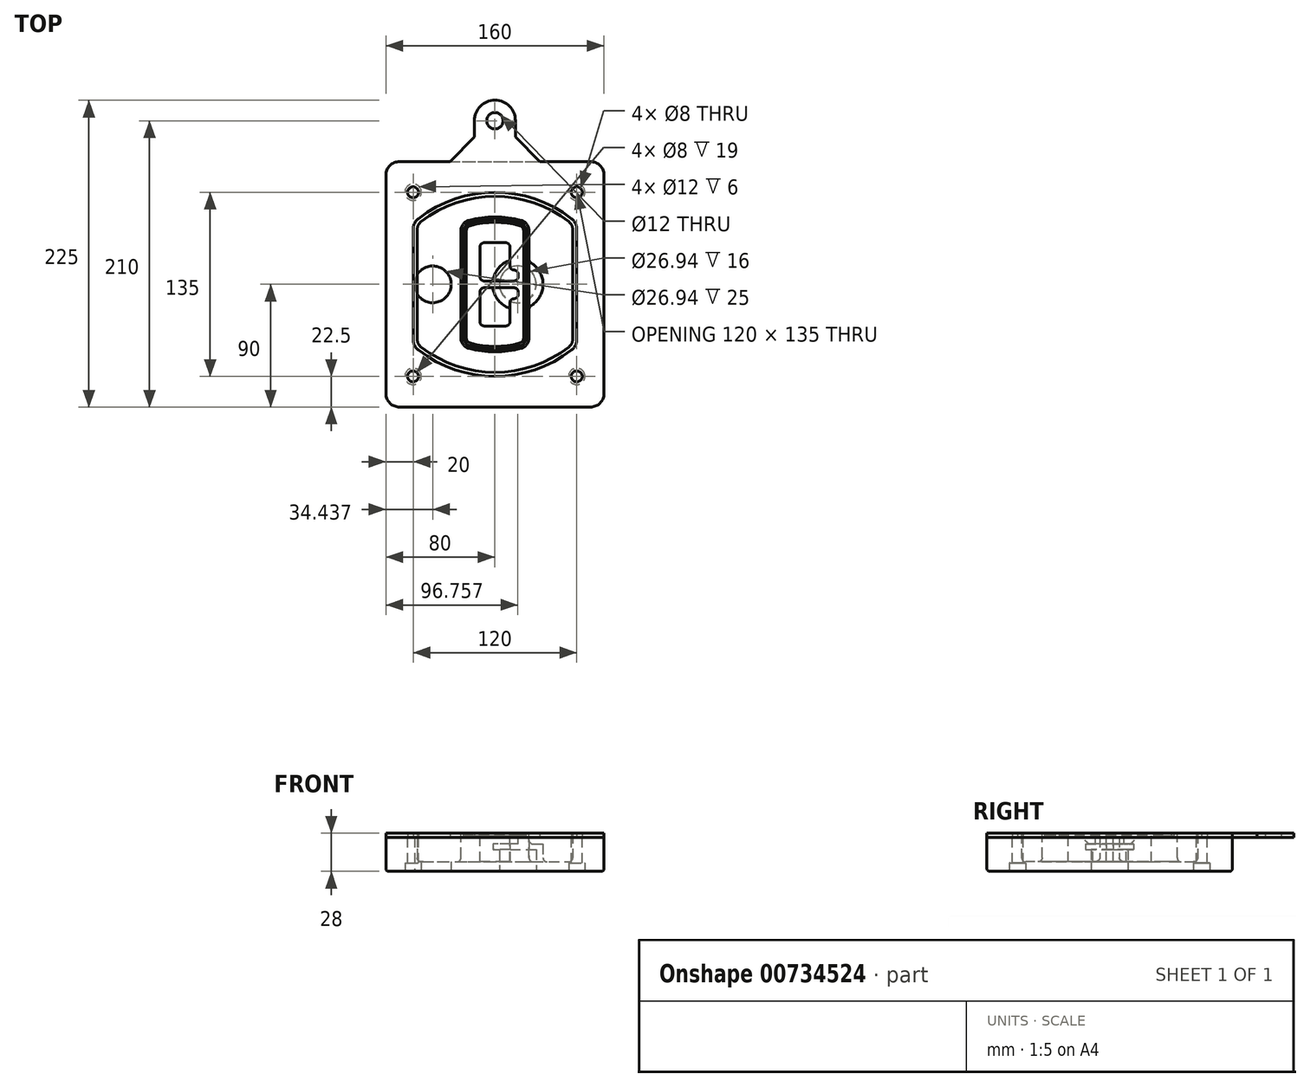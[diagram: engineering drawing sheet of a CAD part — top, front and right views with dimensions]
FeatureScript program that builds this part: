
annotation { "Feature Type Name" : "Feature", "Feature Type Description" : "" }
export const myFeature = defineFeature(function(context is Context, id is Id, definition is map)
    precondition{}
    {
        {
            var Q0;
            Q0=qCreatedBy(makeId("Top.planeOp"),FACE);
            var sketch = newSketch(context, id + "F0", { "sketchPlane" : qUnion([Q0])});
            skPoint(sketch, "E0.rect.middle", {"position": v(0, 0) * mm});
            skLineSegment(sketch, "E1.bottom", {"start": v(-70, -90) * mm, "end": v(70, -90) * mm});
            skLineSegment(sketch, "E1.top", {"start": v(-70, 90) * mm, "end": v(70, 90) * mm});
            skLineSegment(sketch, "E1.left", {"start": v(-80, -80) * mm, "end": v(-80, 80) * mm});
            skLineSegment(sketch, "E1.right", {"start": v(80, -80) * mm, "end": v(80, 80) * mm});
            skLineSegment(sketch, "E2", {"start": v(-80, 90) * mm, "end": v(80, -90) * mm, "construction": true});
            skLineSegment(sketch, "E3", {"start": v(80, 90) * mm, "end": v(-80, -90) * mm, "construction": true});
            skCircle(sketch, "E4", {"center": v(-60, 67.5) * mm, "radius": 4 * mm});
            skCircle(sketch, "E5", {"center": v(60, 67.5) * mm, "radius": 4 * mm});
            skCircle(sketch, "E6", {"center": v(60, -67.5) * mm, "radius": 4 * mm});
            skCircle(sketch, "E7", {"center": v(-60, -67.5) * mm, "radius": 4 * mm});
            skLineSegment(sketch, "E8", {"start": v(-60, 67.5) * mm, "end": v(60, 67.5) * mm, "construction": true});
            skLineSegment(sketch, "E9", {"start": v(60, 67.5) * mm, "end": v(60, -67.5) * mm, "construction": true});
            skLineSegment(sketch, "E10", {"start": v(60, -67.5) * mm, "end": v(-60, -67.5) * mm, "construction": true});
            skLineSegment(sketch, "E11", {"start": v(-60, -67.5) * mm, "end": v(-60, 67.5) * mm, "construction": true});
            skLineSegment(sketch, "E12", {"start": v(-60, 40.3) * mm, "end": v(-60, -40.3) * mm});
            skLineSegment(sketch, "E13", {"start": v(60, 40.3) * mm, "end": v(60, -40.3) * mm});
            skArc(sketch, "E14", {"start": v(56.15, 48.18) * mm, "mid": v(0, 67.5) * mm, "end": v(-56.15, 48.18) * mm});
            skArc(sketch, "E15", {"start": v(-56.15, -48.18) * mm, "mid": v(0, -67.5) * mm, "end": v(56.15, -48.18) * mm});
            skLineSegment(sketch, "E16", {"start": v(-60, 0) * mm, "end": v(60, 0) * mm, "construction": true});
            skPoint(sketch, "E17.visualSharp", {"position": v(-60, -45) * mm});
            skArc(sketch, "E17.filletArc", {"start": v(-60, -40.3) * mm, "mid": v(-58.99, -44.68) * mm, "end": v(-56.15, -48.18) * mm});
            skPoint(sketch, "E18.visualSharp", {"position": v(-60, 45) * mm});
            skArc(sketch, "E18.filletArc", {"start": v(-56.15, 48.18) * mm, "mid": v(-58.99, 44.68) * mm, "end": v(-60, 40.3) * mm});
            skPoint(sketch, "E19.visualSharp", {"position": v(60, 45) * mm});
            skArc(sketch, "E19.filletArc", {"start": v(60, 40.3) * mm, "mid": v(58.99, 44.68) * mm, "end": v(56.15, 48.18) * mm});
            skPoint(sketch, "E20.visualSharp", {"position": v(60, -45) * mm});
            skArc(sketch, "E20.filletArc", {"start": v(56.15, -48.18) * mm, "mid": v(58.99, -44.68) * mm, "end": v(60, -40.3) * mm});
            skPoint(sketch, "E21.visualSharp", {"position": v(-80, 90) * mm});
            skArc(sketch, "E21.filletArc", {"start": v(-70, 90) * mm, "mid": v(-77.07, 87.07) * mm, "end": v(-80, 80) * mm});
            skPoint(sketch, "E22.visualSharp", {"position": v(80, 90) * mm});
            skArc(sketch, "E22.filletArc", {"start": v(80, 80) * mm, "mid": v(77.07, 87.07) * mm, "end": v(70, 90) * mm});
            skPoint(sketch, "E23.visualSharp", {"position": v(80, -90) * mm});
            skArc(sketch, "E23.filletArc", {"start": v(70, -90) * mm, "mid": v(77.07, -87.07) * mm, "end": v(80, -80) * mm});
            skPoint(sketch, "E24.visualSharp", {"position": v(-80, -90) * mm});
            skArc(sketch, "E24.filletArc", {"start": v(-80, -80) * mm, "mid": v(-77.07, -87.07) * mm, "end": v(-70, -90) * mm});
            skArc(sketch, "E25.0", {"start": v(57, 40.3) * mm, "mid": v(56.3, 43.36) * mm, "end": v(54.3, 45.81) * mm});
            skLineSegment(sketch, "E25.1", {"start": v(57, 40.3) * mm, "end": v(57, -40.3) * mm});
            skArc(sketch, "E25.2", {"start": v(54.3, -45.81) * mm, "mid": v(56.3, -43.36) * mm, "end": v(57, -40.3) * mm});
            skArc(sketch, "E25.3", {"start": v(-54.3, -45.81) * mm, "mid": v(0, -64.5) * mm, "end": v(54.3, -45.81) * mm});
            skArc(sketch, "E25.4", {"start": v(-57, -40.3) * mm, "mid": v(-56.3, -43.36) * mm, "end": v(-54.3, -45.81) * mm});
            skArc(sketch, "E25.5", {"start": v(54.3, 45.81) * mm, "mid": v(0, 64.5) * mm, "end": v(-54.3, 45.81) * mm});
            skLineSegment(sketch, "E25.6", {"start": v(-57, 40.3) * mm, "end": v(-57, -40.3) * mm});
            skArc(sketch, "E25.7", {"start": v(-54.3, 45.81) * mm, "mid": v(-56.3, 43.36) * mm, "end": v(-57, 40.3) * mm});
            skArc(sketch, "E26.0", {"start": v(-58.62, 51.33) * mm, "mid": v(-62.58, 46.43) * mm, "end": v(-64, 40.3) * mm});
            skArc(sketch, "E26.1", {"start": v(58.62, 51.33) * mm, "mid": v(0, 71.5) * mm, "end": v(-58.62, 51.33) * mm});
            skArc(sketch, "E26.2", {"start": v(64, 40.3) * mm, "mid": v(62.58, 46.43) * mm, "end": v(58.62, 51.33) * mm});
            skLineSegment(sketch, "E26.3", {"start": v(64, 40.3) * mm, "end": v(64, -40.3) * mm});
            skArc(sketch, "E26.4", {"start": v(58.62, -51.33) * mm, "mid": v(62.58, -46.43) * mm, "end": v(64, -40.3) * mm});
            skLineSegment(sketch, "E26.5", {"start": v(-64, 40.3) * mm, "end": v(-64, -40.3) * mm});
            skArc(sketch, "E26.6", {"start": v(-58.62, -51.33) * mm, "mid": v(0, -71.5) * mm, "end": v(58.62, -51.33) * mm});
            skArc(sketch, "E26.7", {"start": v(-64, -40.3) * mm, "mid": v(-62.58, -46.43) * mm, "end": v(-58.62, -51.33) * mm});
            skSolve(sketch);
        }
        {
            var Q0;
            Q0=makeQuery(id+"F0.imprint","IMPRINT",FACE,{"disambiguationData":[TD([[makeQuery(id+"F0.imprint","IMPRINT",EDGE,{"derivedFrom":sQuery(id+"F0.wireOp",EDGE,"E1.bottom")}),1.0]])]});
            var Q1;
            Q1=makeQuery(id+"F0.imprint","IMPRINT",FACE,{"disambiguationData":[TD([[makeQuery(id+"F0.imprint","IMPRINT",EDGE,{"derivedFrom":sQuery(id+"F0.wireOp",EDGE,"E12")}),1.0]])]});
            var Q2;
            Q2=makeQuery(id+"F0.imprint","IMPRINT",FACE,{"disambiguationData":[TD([[makeQuery(id+"F0.imprint","IMPRINT",EDGE,{"derivedFrom":sQuery(id+"F0.wireOp",EDGE,"E25.0")}),1.0]])]});
            var Q3;
            Q3=makeQuery(id+"F0.imprint","IMPRINT",FACE,{"disambiguationData":[TD([[makeQuery(id+"F0.imprint","IMPRINT",EDGE,{"derivedFrom":sQuery(id+"F0.wireOp",EDGE,"E12")}),-1.0]])]});
            extrude(context, id + "F1", {"entities" : qUnion([Q0, Q1, Q2, Q3]), "oppositeDirection" : true, "depth" : 25 * mm});
        }
        {
            var Q0;
            Q0=makeQuery(id+"F0.imprint","IMPRINT",FACE,{"disambiguationData":[TD([[makeQuery(id+"F0.imprint","IMPRINT",EDGE,{"derivedFrom":sQuery(id+"F0.wireOp",EDGE,"E12")}),1.0]])]});
            extrude(context, id + "F2", {"entities" : qUnion([Q0]), "operationType" : NewBodyOperationType.ADD, "depth" : 3 * mm});
        }
        {
            var Q0;
            Q0=makeQuery(id+"F0.imprint","IMPRINT",FACE,{"disambiguationData":[TD([[makeQuery(id+"F0.imprint","IMPRINT",EDGE,{"derivedFrom":sQuery(id+"F0.wireOp",EDGE,"E25.0")}),1.0]])]});
            extrude(context, id + "F3", {"entities" : qUnion([Q0]), "operationType" : NewBodyOperationType.REMOVE, "oppositeDirection" : true, "depth" : 18 * mm});
        }
        {
            var Q0;
            Q0=makeQuery(id+"F2.opExtrude","CAP_FACE",FACE,{"disambiguationData":[OSD([sQuery(id+"F0.wireOp",EDGE,"E12"),sQuery(id+"F0.wireOp",EDGE,"E13"),sQuery(id+"F0.wireOp",EDGE,"E14"),sQuery(id+"F0.wireOp",EDGE,"E15"),sQuery(id+"F0.wireOp",EDGE,"E17.filletArc"),sQuery(id+"F0.wireOp",EDGE,"E18.filletArc"),sQuery(id+"F0.wireOp",EDGE,"E19.filletArc"),sQuery(id+"F0.wireOp",EDGE,"E20.filletArc"),sQuery(id+"F0.wireOp",EDGE,"E25.0"),sQuery(id+"F0.wireOp",EDGE,"E25.1"),sQuery(id+"F0.wireOp",EDGE,"E25.2"),sQuery(id+"F0.wireOp",EDGE,"E25.3"),sQuery(id+"F0.wireOp",EDGE,"E25.4"),sQuery(id+"F0.wireOp",EDGE,"E25.5"),sQuery(id+"F0.wireOp",EDGE,"E25.6"),sQuery(id+"F0.wireOp",EDGE,"E25.7")])],"isStart":false});
            var sketch = newSketch(context, id + "F4", { "sketchPlane" : qUnion([Q0])});
            skArc(sketch, "E27.0", {"start": v(-19.08, -46.97) * mm, "mid": v(0, -49.5) * mm, "end": v(19.08, -46.97) * mm});
            skArc(sketch, "E28.0", {"start": v(19.08, 46.97) * mm, "mid": v(0, 49.5) * mm, "end": v(-19.08, 46.97) * mm});
            skLineSegment(sketch, "E29", {"start": v(-25, 39.25) * mm, "end": v(-25, -39.25) * mm});
            skLineSegment(sketch, "E30", {"start": v(25, 39.25) * mm, "end": v(25, -39.25) * mm});
            skLineSegment(sketch, "E31", {"start": v(-25, 45.1) * mm, "end": v(25, 45.1) * mm, "construction": true});
            skLineSegment(sketch, "E32", {"start": v(-25, -45.1) * mm, "end": v(25, -45.1) * mm, "construction": true});
            skPoint(sketch, "E33.visualSharp", {"position": v(-25, 45.1) * mm});
            skArc(sketch, "E33.filletArc", {"start": v(-19.08, 46.97) * mm, "mid": v(-23.35, 44.11) * mm, "end": v(-25, 39.25) * mm});
            skPoint(sketch, "E34.visualSharp", {"position": v(25, 45.1) * mm});
            skArc(sketch, "E34.filletArc", {"start": v(25, 39.25) * mm, "mid": v(23.35, 44.11) * mm, "end": v(19.08, 46.97) * mm});
            skPoint(sketch, "E35.visualSharp", {"position": v(25, -45.1) * mm});
            skArc(sketch, "E35.filletArc", {"start": v(19.08, -46.97) * mm, "mid": v(23.35, -44.11) * mm, "end": v(25, -39.25) * mm});
            skPoint(sketch, "E36.visualSharp", {"position": v(-25, -45.1) * mm});
            skArc(sketch, "E36.filletArc", {"start": v(-25, -39.25) * mm, "mid": v(-23.35, -44.11) * mm, "end": v(-19.08, -46.97) * mm});
            skArc(sketch, "E37.0", {"start": v(54.3, 45.81) * mm, "mid": v(0, 64.5) * mm, "end": v(-54.3, 45.81) * mm});
            skArc(sketch, "E37.1", {"start": v(-54.3, 45.81) * mm, "mid": v(-56.3, 43.36) * mm, "end": v(-57, 40.3) * mm});
            skLineSegment(sketch, "E37.2", {"start": v(-57, 40.3) * mm, "end": v(-57, -40.3) * mm});
            skArc(sketch, "E37.3", {"start": v(-57, -40.3) * mm, "mid": v(-56.3, -43.36) * mm, "end": v(-54.3, -45.81) * mm});
            skArc(sketch, "E37.4", {"start": v(-54.3, -45.81) * mm, "mid": v(0, -64.5) * mm, "end": v(54.3, -45.81) * mm});
            skArc(sketch, "E37.5", {"start": v(54.3, -45.81) * mm, "mid": v(56.3, -43.36) * mm, "end": v(57, -40.3) * mm});
            skLineSegment(sketch, "E37.6", {"start": v(57, 40.3) * mm, "end": v(57, -40.3) * mm});
            skArc(sketch, "E37.7", {"start": v(57, 40.3) * mm, "mid": v(56.3, 43.36) * mm, "end": v(54.3, 45.81) * mm});
            skLineSegment(sketch, "E38.0", {"start": v(23, 39.25) * mm, "end": v(23, -39.25) * mm});
            skArc(sketch, "E38.1", {"start": v(18.56, -45.04) * mm, "mid": v(21.76, -42.9) * mm, "end": v(23, -39.25) * mm});
            skArc(sketch, "E38.2", {"start": v(-18.56, -45.04) * mm, "mid": v(0, -47.5) * mm, "end": v(18.56, -45.04) * mm});
            skArc(sketch, "E38.3", {"start": v(-23, -39.25) * mm, "mid": v(-21.76, -42.9) * mm, "end": v(-18.56, -45.04) * mm});
            skLineSegment(sketch, "E38.4", {"start": v(-23, 39.25) * mm, "end": v(-23, -39.25) * mm});
            skArc(sketch, "E38.5", {"start": v(23, 39.25) * mm, "mid": v(21.76, 42.9) * mm, "end": v(18.56, 45.04) * mm});
            skArc(sketch, "E38.6", {"start": v(-18.56, 45.04) * mm, "mid": v(-21.76, 42.9) * mm, "end": v(-23, 39.25) * mm});
            skArc(sketch, "E38.7", {"start": v(18.56, 45.04) * mm, "mid": v(0, 47.5) * mm, "end": v(-18.56, 45.04) * mm});
            skArc(sketch, "E39.0", {"start": v(21, 39.25) * mm, "mid": v(20.18, 41.68) * mm, "end": v(18.04, 43.1) * mm});
            skLineSegment(sketch, "E39.1", {"start": v(21, 39.25) * mm, "end": v(21, -39.25) * mm});
            skArc(sketch, "E39.2", {"start": v(18.04, -43.1) * mm, "mid": v(20.18, -41.68) * mm, "end": v(21, -39.25) * mm});
            skArc(sketch, "E39.3", {"start": v(-18.04, -43.1) * mm, "mid": v(0, -45.5) * mm, "end": v(18.04, -43.1) * mm});
            skArc(sketch, "E39.4", {"start": v(-21, -39.25) * mm, "mid": v(-20.18, -41.68) * mm, "end": v(-18.04, -43.1) * mm});
            skArc(sketch, "E39.5", {"start": v(18.04, 43.1) * mm, "mid": v(0, 45.5) * mm, "end": v(-18.04, 43.1) * mm});
            skLineSegment(sketch, "E39.6", {"start": v(-21, 39.25) * mm, "end": v(-21, -39.25) * mm});
            skArc(sketch, "E39.7", {"start": v(-18.04, 43.1) * mm, "mid": v(-20.18, 41.68) * mm, "end": v(-21, 39.25) * mm});
            skLineSegment(sketch, "E40", {"start": v(-25, 0) * mm, "end": v(25, 0) * mm, "construction": true});
            skLineSegment(sketch, "E41", {"start": v(-11, 5.5) * mm, "end": v(-11, 27.5) * mm});
            skLineSegment(sketch, "E42", {"start": v(-8, 30.5) * mm, "end": v(8, 30.5) * mm});
            skLineSegment(sketch, "E43", {"start": v(11, 27.5) * mm, "end": v(11, 13.5) * mm});
            skLineSegment(sketch, "E44", {"start": v(14, 10.5) * mm, "end": v(14, 10.5) * mm});
            skLineSegment(sketch, "E45", {"start": v(17, 7.5) * mm, "end": v(17, 5.5) * mm});
            skLineSegment(sketch, "E46", {"start": v(14, 2.5) * mm, "end": v(-8, 2.5) * mm});
            skPoint(sketch, "E47.visualSharp", {"position": v(-11, 30.5) * mm});
            skArc(sketch, "E47.filletArc", {"start": v(-8, 30.5) * mm, "mid": v(-10.12, 29.62) * mm, "end": v(-11, 27.5) * mm});
            skPoint(sketch, "E48.visualSharp", {"position": v(11, 30.5) * mm});
            skArc(sketch, "E48.filletArc", {"start": v(11, 27.5) * mm, "mid": v(10.12, 29.62) * mm, "end": v(8, 30.5) * mm});
            skPoint(sketch, "E49.visualSharp", {"position": v(11, 10.5) * mm});
            skArc(sketch, "E49.filletArc", {"start": v(11, 13.5) * mm, "mid": v(11.88, 11.38) * mm, "end": v(14, 10.5) * mm});
            skPoint(sketch, "E50.visualSharp", {"position": v(17, 10.5) * mm});
            skArc(sketch, "E50.filletArc", {"start": v(17, 7.5) * mm, "mid": v(16.12, 9.62) * mm, "end": v(14, 10.5) * mm});
            skPoint(sketch, "E51.visualSharp", {"position": v(17, 2.5) * mm});
            skArc(sketch, "E51.filletArc", {"start": v(14, 2.5) * mm, "mid": v(16.12, 3.38) * mm, "end": v(17, 5.5) * mm});
            skPoint(sketch, "E52.visualSharp", {"position": v(-11, 2.5) * mm});
            skArc(sketch, "E52.filletArc", {"start": v(-11, 5.5) * mm, "mid": v(-10.12, 3.38) * mm, "end": v(-8, 2.5) * mm});
            skLineSegment(sketch, "E53.0.MirrorCS", {"start": v(14, -2.5) * mm, "end": v(-8, -2.5) * mm});
            skArc(sketch, "E54.0.MirrorCS", {"start": v(-11, -5.5) * mm, "mid": v(-10.12, -3.38) * mm, "end": v(-8, -2.5) * mm});
            skLineSegment(sketch, "E55.0.MirrorCS", {"start": v(-11, -5.5) * mm, "end": v(-11, -27.5) * mm});
            skArc(sketch, "E56.0.MirrorCS", {"start": v(-8, -30.5) * mm, "mid": v(-10.12, -29.62) * mm, "end": v(-11, -27.5) * mm});
            skLineSegment(sketch, "E57.0.MirrorCS", {"start": v(-8, -30.5) * mm, "end": v(8, -30.5) * mm});
            skArc(sketch, "E58.0.MirrorCS", {"start": v(11, -27.5) * mm, "mid": v(10.12, -29.62) * mm, "end": v(8, -30.5) * mm});
            skLineSegment(sketch, "E59.0.MirrorCS", {"start": v(11, -27.5) * mm, "end": v(11, -13.5) * mm});
            skArc(sketch, "E60.0.MirrorCS", {"start": v(11, -13.5) * mm, "mid": v(11.88, -11.38) * mm, "end": v(14, -10.5) * mm});
            skArc(sketch, "E61.0.MirrorCS", {"start": v(17, -7.5) * mm, "mid": v(16.12, -9.62) * mm, "end": v(14, -10.5) * mm});
            skLineSegment(sketch, "E62.0.MirrorCS", {"start": v(17, -7.5) * mm, "end": v(17, -5.5) * mm});
            skArc(sketch, "E63.0.MirrorCS", {"start": v(14, -2.5) * mm, "mid": v(16.12, -3.38) * mm, "end": v(17, -5.5) * mm});
            skSolve(sketch);
        }
        {
            var Q0;
            Q0=makeQuery(id+"F4.imprint","IMPRINT",FACE,{"disambiguationData":[TD([[makeQuery(id+"F4.imprint","IMPRINT",EDGE,{"derivedFrom":sQuery(id+"F4.wireOp",EDGE,"E27.0")}),1.0]])]});
            var Q1;
            Q1=makeQuery(id+"F4.imprint","IMPRINT",FACE,{"disambiguationData":[TD([[makeQuery(id+"F4.imprint","IMPRINT",EDGE,{"derivedFrom":sQuery(id+"F4.wireOp",EDGE,"E38.0")}),-1.0]])]});
            var Q2;
            Q2=makeQuery(id+"F4.imprint","IMPRINT",FACE,{"disambiguationData":[TD([[makeQuery(id+"F4.imprint","IMPRINT",EDGE,{"derivedFrom":sQuery(id+"F4.wireOp",EDGE,"E39.0")}),1.0]])]});
            extrude(context, id + "F5", {"entities" : qUnion([Q0, Q1, Q2]), "operationType" : NewBodyOperationType.ADD, "endBound" : BoundingType.UP_TO_NEXT, "oppositeDirection" : true, "depth" : 25 * mm});
        }
        {
            var Q0;
            Q0=makeQuery(id+"F4.imprint","IMPRINT",FACE,{"disambiguationData":[TD([[makeQuery(id+"F4.imprint","IMPRINT",EDGE,{"derivedFrom":sQuery(id+"F4.wireOp",EDGE,"E38.0")}),-1.0]])]});
            extrude(context, id + "F6", {"entities" : qUnion([Q0]), "operationType" : NewBodyOperationType.REMOVE, "oppositeDirection" : true, "depth" : 2 * mm});
        }
        {
            var Q0;
            Q0=makeQuery(id+"F1.opExtrude","CAP_FACE",FACE,{"disambiguationData":[OSD([sQuery(id+"F0.wireOp",EDGE,"E1.bottom"),sQuery(id+"F0.wireOp",EDGE,"E1.top"),sQuery(id+"F0.wireOp",EDGE,"E1.left"),sQuery(id+"F0.wireOp",EDGE,"E1.right"),sQuery(id+"F0.wireOp",EDGE,"E4"),sQuery(id+"F0.wireOp",EDGE,"E5"),sQuery(id+"F0.wireOp",EDGE,"E6"),sQuery(id+"F0.wireOp",EDGE,"E7"),sQuery(id+"F0.wireOp",EDGE,"E21.filletArc"),sQuery(id+"F0.wireOp",EDGE,"E22.filletArc"),sQuery(id+"F0.wireOp",EDGE,"E23.filletArc"),sQuery(id+"F0.wireOp",EDGE,"E24.filletArc")])],"isStart":false});
            var sketch = newSketch(context, id + "F7", { "sketchPlane" : qUnion([Q0])});
            skCircle(sketch, "E64", {"center": v(16.76, 0) * mm, "radius": 13.47 * mm});
            skCircle(sketch, "E65", {"center": v(-45.56, 0) * mm, "radius": 13.47 * mm});
            skLineSegment(sketch, "E66", {"start": v(80, 0) * mm, "end": v(-80, 0) * mm});
            skCircle(sketch, "E67", {"center": v(16.76, 0) * mm, "radius": 18.47 * mm});
            skCircle(sketch, "E68", {"center": v(60, -67.5) * mm, "radius": 6 * mm});
            skCircle(sketch, "E69", {"center": v(-60, -67.5) * mm, "radius": 6 * mm});
            skCircle(sketch, "E70", {"center": v(-60, 67.5) * mm, "radius": 6 * mm});
            skCircle(sketch, "E71", {"center": v(60, 67.5) * mm, "radius": 6 * mm});
            skSolve(sketch);
        }
        {
            var Q0;
            {var subQ1=sQuery(id+"F7.wireOp",EDGE,"E66");var subQ4=sQuery(id+"F7.wireOp",EDGE,"E64");var subQ6=makeQuery(id+"F7.imprint","INTERSECT",VERTEX,{"disambiguationData":[OD(0.0)],"derivedFrom":[subQ4,subQ1]});Q0=makeQuery(id+"F7.imprint","IMPRINT",FACE,{"disambiguationData":[TD([[makeQuery(id+"F7.imprint","IMPRINT",EDGE,{"disambiguationData":[TD([[subQ6,-1.0]])],"derivedFrom":subQ4}),-1.0]])]});}
            var Q1;
            {var subQ0=sQuery(id+"F7.wireOp",EDGE,"E66");var subQ1=sQuery(id+"F7.wireOp",EDGE,"E64");var subQ3=makeQuery(id+"F7.imprint","INTERSECT",VERTEX,{"disambiguationData":[OD(0.0)],"derivedFrom":[subQ1,subQ0]});Q1=makeQuery(id+"F7.imprint","IMPRINT",FACE,{"disambiguationData":[TD([[makeQuery(id+"F7.imprint","IMPRINT",EDGE,{"disambiguationData":[TD([[subQ3,-1.0]])],"derivedFrom":subQ1}),1.0]])]});}
            var Q2;
            {var subQ0=sQuery(id+"F7.wireOp",EDGE,"E66");var subQ1=sQuery(id+"F7.wireOp",EDGE,"E64");var subQ3=makeQuery(id+"F7.imprint","INTERSECT",VERTEX,{"disambiguationData":[OD(0.0)],"derivedFrom":[subQ1,subQ0]});Q2=makeQuery(id+"F7.imprint","IMPRINT",FACE,{"disambiguationData":[TD([[makeQuery(id+"F7.imprint","IMPRINT",EDGE,{"disambiguationData":[TD([[subQ3,1.0]])],"derivedFrom":subQ1}),1.0]])]});}
            var Q3;
            {var subQ1=sQuery(id+"F7.wireOp",EDGE,"E66");var subQ4=sQuery(id+"F7.wireOp",EDGE,"E64");var subQ6=makeQuery(id+"F7.imprint","INTERSECT",VERTEX,{"disambiguationData":[OD(0.0)],"derivedFrom":[subQ4,subQ1]});Q3=makeQuery(id+"F7.imprint","IMPRINT",FACE,{"disambiguationData":[TD([[makeQuery(id+"F7.imprint","IMPRINT",EDGE,{"disambiguationData":[TD([[subQ6,1.0]])],"derivedFrom":subQ4}),-1.0]])]});}
            extrude(context, id + "F8", {"entities" : qUnion([Q0, Q1, Q2, Q3]), "operationType" : NewBodyOperationType.ADD, "oppositeDirection" : true, "depth" : 20 * mm});
        }
        {
            var Q0;
            {var subQ0=sQuery(id+"F7.wireOp",EDGE,"E66");var subQ1=sQuery(id+"F7.wireOp",EDGE,"E64");var subQ3=makeQuery(id+"F7.imprint","INTERSECT",VERTEX,{"disambiguationData":[OD(0.0)],"derivedFrom":[subQ1,subQ0]});Q0=makeQuery(id+"F7.imprint","IMPRINT",FACE,{"disambiguationData":[TD([[makeQuery(id+"F7.imprint","IMPRINT",EDGE,{"disambiguationData":[TD([[subQ3,-1.0]])],"derivedFrom":subQ1}),1.0]])]});}
            var Q1;
            {var subQ0=sQuery(id+"F7.wireOp",EDGE,"E66");var subQ1=sQuery(id+"F7.wireOp",EDGE,"E64");var subQ3=makeQuery(id+"F7.imprint","INTERSECT",VERTEX,{"disambiguationData":[OD(0.0)],"derivedFrom":[subQ1,subQ0]});Q1=makeQuery(id+"F7.imprint","IMPRINT",FACE,{"disambiguationData":[TD([[makeQuery(id+"F7.imprint","IMPRINT",EDGE,{"disambiguationData":[TD([[subQ3,1.0]])],"derivedFrom":subQ1}),1.0]])]});}
            extrude(context, id + "F9", {"entities" : qUnion([Q0, Q1]), "operationType" : NewBodyOperationType.REMOVE, "oppositeDirection" : true, "depth" : 16 * mm});
        }
        {
            var Q0;
            {var subQ0=sQuery(id+"F7.wireOp",EDGE,"E66");var subQ1=sQuery(id+"F7.wireOp",EDGE,"E65");var subQ3=makeQuery(id+"F7.imprint","INTERSECT",VERTEX,{"disambiguationData":[OD(0.0)],"derivedFrom":[subQ1,subQ0]});Q0=makeQuery(id+"F7.imprint","IMPRINT",FACE,{"disambiguationData":[TD([[makeQuery(id+"F7.imprint","IMPRINT",EDGE,{"disambiguationData":[TD([[subQ3,-1.0]])],"derivedFrom":subQ1}),1.0]])]});}
            var Q1;
            {var subQ0=sQuery(id+"F7.wireOp",EDGE,"E66");var subQ1=sQuery(id+"F7.wireOp",EDGE,"E65");var subQ3=makeQuery(id+"F7.imprint","INTERSECT",VERTEX,{"disambiguationData":[OD(0.0)],"derivedFrom":[subQ1,subQ0]});Q1=makeQuery(id+"F7.imprint","IMPRINT",FACE,{"disambiguationData":[TD([[makeQuery(id+"F7.imprint","IMPRINT",EDGE,{"disambiguationData":[TD([[subQ3,1.0]])],"derivedFrom":subQ1}),1.0]])]});}
            extrude(context, id + "F10", {"entities" : qUnion([Q0, Q1]), "operationType" : NewBodyOperationType.REMOVE, "oppositeDirection" : true, "depth" : 25 * mm});
        }
        {
            var Q0;
            Q0=makeQuery(id+"F7.imprint","IMPRINT",FACE,{"disambiguationData":[TD([[makeQuery(id+"F7.imprint","IMPRINT",EDGE,{"derivedFrom":sQuery(id+"F7.wireOp",EDGE,"E68")}),1.0]])]});
            var Q1;
            Q1=makeQuery(id+"F7.imprint","IMPRINT",FACE,{"disambiguationData":[TD([[makeQuery(id+"F7.imprint","IMPRINT",EDGE,{"derivedFrom":makeQuery(id+"F1.opExtrude","CAP_EDGE",EDGE,{"disambiguationData":[OSD([sQuery(id+"F0.wireOp",EDGE,"E5")])],"isStart":false})}),-1.0]])]});
            var Q2;
            Q2=makeQuery(id+"F7.imprint","IMPRINT",FACE,{"disambiguationData":[TD([[makeQuery(id+"F7.imprint","IMPRINT",EDGE,{"derivedFrom":sQuery(id+"F7.wireOp",EDGE,"E69")}),1.0]])]});
            var Q3;
            Q3=makeQuery(id+"F7.imprint","IMPRINT",FACE,{"disambiguationData":[TD([[makeQuery(id+"F7.imprint","IMPRINT",EDGE,{"derivedFrom":makeQuery(id+"F1.opExtrude","CAP_EDGE",EDGE,{"disambiguationData":[OSD([sQuery(id+"F0.wireOp",EDGE,"E4")])],"isStart":false})}),-1.0]])]});
            var Q4;
            Q4=makeQuery(id+"F7.imprint","IMPRINT",FACE,{"disambiguationData":[TD([[makeQuery(id+"F7.imprint","IMPRINT",EDGE,{"derivedFrom":sQuery(id+"F7.wireOp",EDGE,"E70")}),1.0]])]});
            var Q5;
            Q5=makeQuery(id+"F7.imprint","IMPRINT",FACE,{"disambiguationData":[TD([[makeQuery(id+"F7.imprint","IMPRINT",EDGE,{"derivedFrom":makeQuery(id+"F1.opExtrude","CAP_EDGE",EDGE,{"disambiguationData":[OSD([sQuery(id+"F0.wireOp",EDGE,"E7")])],"isStart":false})}),-1.0]])]});
            var Q6;
            Q6=makeQuery(id+"F7.imprint","IMPRINT",FACE,{"disambiguationData":[TD([[makeQuery(id+"F7.imprint","IMPRINT",EDGE,{"derivedFrom":sQuery(id+"F7.wireOp",EDGE,"E71")}),1.0]])]});
            var Q7;
            Q7=makeQuery(id+"F7.imprint","IMPRINT",FACE,{"disambiguationData":[TD([[makeQuery(id+"F7.imprint","IMPRINT",EDGE,{"derivedFrom":makeQuery(id+"F1.opExtrude","CAP_EDGE",EDGE,{"disambiguationData":[OSD([sQuery(id+"F0.wireOp",EDGE,"E6")])],"isStart":false})}),-1.0]])]});
            extrude(context, id + "F11", {"entities" : qUnion([Q0, Q1, Q2, Q3, Q4, Q5, Q6, Q7]), "operationType" : NewBodyOperationType.REMOVE, "oppositeDirection" : true, "depth" : 6 * mm});
        }
        {
            var Q0;
            Q0=makeQuery(id+"F9.boolean.opBoolean","COPY",FACE,{"derivedFrom":makeQuery(id+"F9.opExtrude","CAP_FACE",FACE,{"disambiguationData":[OSD([sQuery(id+"F7.wireOp",EDGE,"E64")])],"isStart":false})});
            var sketch = newSketch(context, id + "F12", { "sketchPlane" : qUnion([Q0])});
            skArc(sketch, "E72.0", {"start": v(11, 17.55) * mm, "mid": v(2.57, 11.82) * mm, "end": v(-1.54, 2.5) * mm});
            skArc(sketch, "E72.1", {"start": v(-1.54, -2.5) * mm, "mid": v(2.57, -11.82) * mm, "end": v(11, -17.55) * mm});
            skLineSegment(sketch, "E73", {"start": v(-1.54, -2.5) * mm, "end": v(14, -2.5) * mm});
            skLineSegment(sketch, "E74.0", {"start": v(14, 2.5) * mm, "end": v(-1.54, 2.5) * mm});
            skArc(sketch, "E74.1", {"start": v(14, 2.5) * mm, "mid": v(16.12, 3.38) * mm, "end": v(17, 5.5) * mm});
            skLineSegment(sketch, "E74.2", {"start": v(17, 7.5) * mm, "end": v(17, 5.5) * mm});
            skArc(sketch, "E74.3", {"start": v(17, 7.5) * mm, "mid": v(16.12, 9.62) * mm, "end": v(14, 10.5) * mm});
            skArc(sketch, "E74.4", {"start": v(11, 13.5) * mm, "mid": v(11.88, 11.38) * mm, "end": v(14, 10.5) * mm});
            skLineSegment(sketch, "E74.5", {"start": v(11, 17.55) * mm, "end": v(11, 13.5) * mm});
            skLineSegment(sketch, "E74.7", {"start": v(14, -2.5) * mm, "end": v(-1.54, -2.5) * mm});
            skArc(sketch, "E74.8", {"start": v(14, -2.5) * mm, "mid": v(16.12, -3.38) * mm, "end": v(17, -5.5) * mm});
            skLineSegment(sketch, "E74.9", {"start": v(17, -7.5) * mm, "end": v(17, -5.5) * mm});
            skArc(sketch, "E74.10", {"start": v(17, -7.5) * mm, "mid": v(16.12, -9.62) * mm, "end": v(14, -10.5) * mm});
            skArc(sketch, "E74.11", {"start": v(11, -13.5) * mm, "mid": v(11.88, -11.38) * mm, "end": v(14, -10.5) * mm});
            skLineSegment(sketch, "E74.12", {"start": v(11, -17.55) * mm, "end": v(11, -13.5) * mm});
            skPoint(sketch, "E75.orphan", {"position": v(11, -27.5) * mm});
            skPoint(sketch, "E76.orphan", {"position": v(-8, -2.5) * mm});
            skPoint(sketch, "E77.orphan", {"position": v(-8, 2.5) * mm});
            skPoint(sketch, "E78.orphan", {"position": v(11, 27.5) * mm});
            skSolve(sketch);
        }
        {
            var Q0;
            {var subQ7=sQuery(id+"F12.wireOp",EDGE,"E72.0");var subQ14=sQuery(id+"F12.wireOp",EDGE,"E72.1");var subQ16=sQuery(id+"F12.wireOp",EDGE,"E74.1");var subQ18=sQuery(id+"F12.wireOp",EDGE,"E74.8");Q0=qUnion([makeQuery(id+"F12.imprint","IMPRINT",FACE,{"disambiguationData":[TD([[makeQuery(id+"F12.imprint","IMPRINT",EDGE,{"derivedFrom":subQ7}),1.0]])]}),makeQuery(id+"F12.imprint","IMPRINT",FACE,{"disambiguationData":[TD([[makeQuery(id+"F12.imprint","IMPRINT",EDGE,{"derivedFrom":subQ14}),1.0]])]}),makeQuery(id+"F12.imprint","IMPRINT",FACE,{"disambiguationData":[TD([[makeQuery(id+"F12.imprint","IMPRINT",EDGE,{"derivedFrom":subQ16}),1.0]])]}),makeQuery(id+"F12.imprint","IMPRINT",FACE,{"disambiguationData":[TD([[makeQuery(id+"F12.imprint","IMPRINT",EDGE,{"derivedFrom":subQ18}),-1.0]])]})]);}
            var Q1;
            Q1=makeQuery(id+"F5.boolean.opBoolean","SPLIT",FACE,{"disambiguationData":[TD([makeQuery(id+"F5.opExtrude","SWEPT_FACE",FACE,{"disambiguationData":[OSD([sQuery(id+"F4.wireOp",EDGE,"E41")])]})])],"derivedFrom":makeQuery(id+"F3.boolean.opBoolean","COPY",FACE,{"derivedFrom":makeQuery(id+"F3.opExtrude","CAP_FACE",FACE,{"disambiguationData":[OSD([sQuery(id+"F0.wireOp",EDGE,"E25.0"),sQuery(id+"F0.wireOp",EDGE,"E25.1"),sQuery(id+"F0.wireOp",EDGE,"E25.2"),sQuery(id+"F0.wireOp",EDGE,"E25.3"),sQuery(id+"F0.wireOp",EDGE,"E25.4"),sQuery(id+"F0.wireOp",EDGE,"E25.5"),sQuery(id+"F0.wireOp",EDGE,"E25.6"),sQuery(id+"F0.wireOp",EDGE,"E25.7")])],"isStart":false})})});
            extrude(context, id + "F13", {"entities" : qUnion([Q0]), "operationType" : NewBodyOperationType.REMOVE, "endBound" : BoundingType.UP_TO_SURFACE, "endBoundEntityFace" : qUnion([Q1]), "depth" : 25 * mm});
        }
        {
            var Q0;
            Q0=makeQuery(id+"F3.boolean.opBoolean","COPY",EDGE,{"derivedFrom":makeQuery(id+"F3.opExtrude","CAP_EDGE",EDGE,{"disambiguationData":[OSD([sQuery(id+"F0.wireOp",EDGE,"E25.6")])],"isStart":false})});
            var Q1;
            Q1=makeQuery(id+"F8.boolean.opBoolean","INTERSECT",EDGE,{"derivedFrom":[makeQuery(id+"F5.opExtrude","SWEPT_FACE",FACE,{"disambiguationData":[OSD([sQuery(id+"F4.wireOp",EDGE,"E30")])]}),makeQuery(id+"F8.opExtrude","CAP_FACE",FACE,{"disambiguationData":[OSD([sQuery(id+"F7.wireOp",EDGE,"E67")])],"isStart":false})]});
            var Q2;
            Q2=makeQuery(id+"F8.boolean.opBoolean","INTERSECT",EDGE,{"disambiguationData":[OD(1.0)],"derivedFrom":[makeQuery(id+"F5.opExtrude","SWEPT_FACE",FACE,{"disambiguationData":[OSD([sQuery(id+"F4.wireOp",EDGE,"E30")])]}),makeQuery(id+"F8.opExtrude","SWEPT_FACE",FACE,{"disambiguationData":[OSD([sQuery(id+"F7.wireOp",EDGE,"E67")])]})]});
            var Q3;
            {var subQ0=sQuery(id+"F4.wireOp",EDGE,"E30");Q3=makeQuery(id+"F8.boolean.opBoolean","SPLIT",EDGE,{"disambiguationData":[TD([makeQuery(id+"F5.opExtrude","SWEPT_FACE",FACE,{"disambiguationData":[OSD([sQuery(id+"F4.wireOp",EDGE,"E35.filletArc")])]})])],"derivedFrom":makeQuery(id+"F5.opExtrude","CAP_EDGE",EDGE,{"disambiguationData":[OSD([subQ0])],"isStart":false})});}
            var Q4;
            {var subQ0=sQuery(id+"F0.wireOp",EDGE,"E25.7");var subQ1=sQuery(id+"F0.wireOp",EDGE,"E25.1");var subQ2=sQuery(id+"F0.wireOp",EDGE,"E25.6");var subQ3=sQuery(id+"F0.wireOp",EDGE,"E25.5");var subQ4=sQuery(id+"F0.wireOp",EDGE,"E25.4");var subQ5=sQuery(id+"F0.wireOp",EDGE,"E25.0");var subQ6=sQuery(id+"F0.wireOp",EDGE,"E25.2");var subQ7=sQuery(id+"F0.wireOp",EDGE,"E25.3");Q4=makeQuery(id+"F8.boolean.opBoolean","INTERSECT",EDGE,{"derivedFrom":[makeQuery(id+"F5.boolean.opBoolean","SPLIT",FACE,{"disambiguationData":[TD([makeQuery(id+"F2.opExtrude","SWEPT_FACE",FACE,{"disambiguationData":[OSD([subQ5])]})])],"derivedFrom":makeQuery(id+"F3.boolean.opBoolean","COPY",FACE,{"derivedFrom":makeQuery(id+"F3.opExtrude","CAP_FACE",FACE,{"disambiguationData":[OSD([subQ5,subQ1,subQ6,subQ7,subQ4,subQ3,subQ2,subQ0])],"isStart":false})})}),makeQuery(id+"F8.opExtrude","SWEPT_FACE",FACE,{"disambiguationData":[OSD([sQuery(id+"F7.wireOp",EDGE,"E67")])]})]});}
            var Q5;
            Q5=makeQuery(id+"F8.boolean.opBoolean","INTERSECT",EDGE,{"disambiguationData":[OD(0.0)],"derivedFrom":[makeQuery(id+"F5.opExtrude","SWEPT_FACE",FACE,{"disambiguationData":[OSD([sQuery(id+"F4.wireOp",EDGE,"E30")])]}),makeQuery(id+"F8.opExtrude","SWEPT_FACE",FACE,{"disambiguationData":[OSD([sQuery(id+"F7.wireOp",EDGE,"E67")])]})]});
            fillet(context, id + "F14", {"entities" : qUnion([Q0, Q1, Q2, Q3, Q4, Q5]), "radius" : 3 * mm, "tangentPropagation" : true, "allowEdgeOverflow" : false});
        }
        {
            var Q0;
            Q0=makeQuery(id+"F1.opExtrude","CAP_EDGE",EDGE,{"disambiguationData":[OSD([sQuery(id+"F0.wireOp",EDGE,"E1.bottom")])],"isStart":false});
            fillet(context, id + "F15", {"entities" : qUnion([Q0]), "radius" : 2 * mm, "tangentPropagation" : true, "allowEdgeOverflow" : false});
        }
        {
            var Q0;
            {var subQ0=sQuery(id+"F0.wireOp",EDGE,"E21.filletArc");var subQ1=sQuery(id+"F0.wireOp",EDGE,"E7");var subQ2=sQuery(id+"F0.wireOp",EDGE,"E6");var subQ3=sQuery(id+"F0.wireOp",EDGE,"E5");var subQ4=sQuery(id+"F0.wireOp",EDGE,"E4");var subQ5=sQuery(id+"F0.wireOp",EDGE,"E22.filletArc");var subQ6=sQuery(id+"F0.wireOp",EDGE,"E1.bottom");var subQ7=sQuery(id+"F0.wireOp",EDGE,"E1.right");var subQ8=sQuery(id+"F0.wireOp",EDGE,"E1.top");var subQ9=sQuery(id+"F0.wireOp",EDGE,"E1.left");var subQ10=sQuery(id+"F0.wireOp",EDGE,"E23.filletArc");var subQ11=sQuery(id+"F0.wireOp",EDGE,"E24.filletArc");Q0=makeQuery(id+"F2.boolean.opBoolean","SPLIT",FACE,{"disambiguationData":[TD([makeQuery(id+"F1.opExtrude","SWEPT_FACE",FACE,{"disambiguationData":[OSD([subQ6])]})])],"derivedFrom":makeQuery(id+"F1.opExtrude","CAP_FACE",FACE,{"disambiguationData":[OSD([subQ6,subQ8,subQ9,subQ7,subQ4,subQ3,subQ2,subQ1,subQ0,subQ5,subQ10,subQ11])],"isStart":true})});}
            var sketch = newSketch(context, id + "F16", { "sketchPlane" : qUnion([Q0])});
            skCircle(sketch, "E79", {"center": v(0, 120) * mm, "radius": 6 * mm});
            skPoint(sketch, "E79.centerSnap0", {"position": v(0, 90) * mm});
            skArc(sketch, "E80", {"start": v(15, 120) * mm, "mid": v(0, 135) * mm, "end": v(-15, 120) * mm});
            skLineSegment(sketch, "E81", {"start": v(-15, 120) * mm, "end": v(-15, 108) * mm});
            skLineSegment(sketch, "E82", {"start": v(15, 120) * mm, "end": v(15, 108) * mm});
            skLineSegment(sketch, "E83", {"start": v(15, 108) * mm, "end": v(33, 90) * mm});
            skLineSegment(sketch, "E84", {"start": v(-15, 108) * mm, "end": v(-33, 90) * mm});
            skLineSegment(sketch, "E85", {"start": v(-80, 0) * mm, "end": v(80, 0) * mm, "construction": true});
            skArc(sketch, "E86.MirrorCS", {"start": v(15, -120) * mm, "mid": v(0, -135) * mm, "end": v(-15, -120) * mm});
            skCircle(sketch, "E87.MirrorC", {"center": v(0, -120) * mm, "radius": 6 * mm});
            skLineSegment(sketch, "E88.MirrorCS", {"start": v(-15, -120) * mm, "end": v(-15, -108) * mm});
            skLineSegment(sketch, "E89.MirrorCS", {"start": v(15, -120) * mm, "end": v(15, -108) * mm});
            skLineSegment(sketch, "E90.MirrorCS", {"start": v(15, -108) * mm, "end": v(33, -90) * mm});
            skLineSegment(sketch, "E91.MirrorCS", {"start": v(-15, -108) * mm, "end": v(-33, -90) * mm});
            skSolve(sketch);
        }
        {
            var Q0;
            Q0=makeQuery(id+"F16.imprint","IMPRINT",FACE,{"disambiguationData":[TD([[makeQuery(id+"F16.imprint","IMPRINT",EDGE,{"derivedFrom":sQuery(id+"F16.wireOp",EDGE,"E86.MirrorCS")}),-1.0]])]});
            var Q1;
            Q1=makeQuery(id+"F16.imprint","IMPRINT",FACE,{"disambiguationData":[TD([[makeQuery(id+"F16.imprint","IMPRINT",EDGE,{"derivedFrom":sQuery(id+"F16.wireOp",EDGE,"E79")}),-1.0]])]});
            var Q2;
            Q2=makeQuery(id+"F16.imprint","IMPRINT",FACE,{"disambiguationData":[TD([[makeQuery(id+"F16.imprint","IMPRINT",EDGE,{"derivedFrom":makeQuery(id+"F1.opExtrude","CAP_EDGE",EDGE,{"disambiguationData":[OSD([sQuery(id+"F0.wireOp",EDGE,"E1.left")])],"isStart":true})}),-1.0]])]});
            var Q3;
            Q3=makeQuery(id+"F2.opExtrude","CAP_FACE",FACE,{"disambiguationData":[OSD([sQuery(id+"F0.wireOp",EDGE,"E12"),sQuery(id+"F0.wireOp",EDGE,"E13"),sQuery(id+"F0.wireOp",EDGE,"E14"),sQuery(id+"F0.wireOp",EDGE,"E15"),sQuery(id+"F0.wireOp",EDGE,"E17.filletArc"),sQuery(id+"F0.wireOp",EDGE,"E18.filletArc"),sQuery(id+"F0.wireOp",EDGE,"E19.filletArc"),sQuery(id+"F0.wireOp",EDGE,"E20.filletArc"),sQuery(id+"F0.wireOp",EDGE,"E25.0"),sQuery(id+"F0.wireOp",EDGE,"E25.1"),sQuery(id+"F0.wireOp",EDGE,"E25.2"),sQuery(id+"F0.wireOp",EDGE,"E25.3"),sQuery(id+"F0.wireOp",EDGE,"E25.4"),sQuery(id+"F0.wireOp",EDGE,"E25.5"),sQuery(id+"F0.wireOp",EDGE,"E25.6"),sQuery(id+"F0.wireOp",EDGE,"E25.7")])],"isStart":false});
            extrude(context, id + "F17", {"entities" : qUnion([Q0, Q1, Q2]), "endBound" : BoundingType.UP_TO_SURFACE, "depth" : 25 * mm, "endBoundEntityFace" : qUnion([Q3]), "offsetDistance" : 25 * mm});
        }
    });
